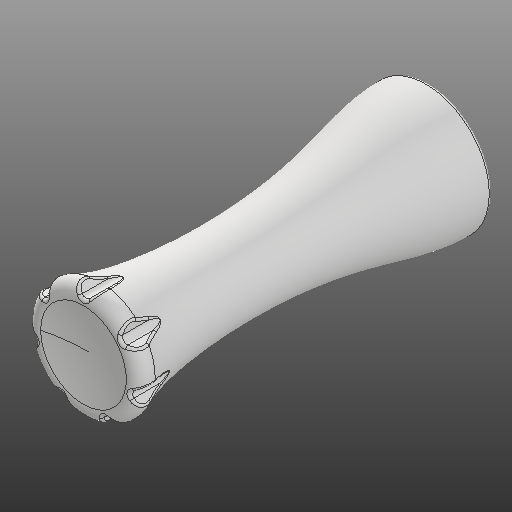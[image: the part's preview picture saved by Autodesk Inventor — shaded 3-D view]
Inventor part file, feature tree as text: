
AUTODESK INVENTOR PART (.ipt)
format: ipt  version: 2020 (Build 240168000, 168)  size: 590,336 bytes
history: native  units: in
note: dims shown in document units (in); Inventor stores cm internally (conversion verified against a paired STEP export)
features: fillet x2, sketch x2, revolve x1, extrude x1, pattern_circular x1
ambient origin geometry x8: Origin, YZ Plane, XZ Plane, XY Plane, X Axis, Y Axis, Z Axis, Center Point
bodies: Solid1 (feature_tree)
feature tree (7):
  revolve  "Revolution1"  [1 undecoded]
  extrude  "Extrusion1"  TaperAngle=90.0deg  [1 undecoded]
  pattern_circular  "Circular Pattern1"  [2 undecoded]
  fillet  "Fillet1"  Radius=0.2756in
  fillet  "Fillet3"  Radius=0.0984in
  sketch  "Sketch2"  dims[d1=0.2203in d4=0.0394in]
  sketch  "Sketch3"  dims[d6=1.1811in d7=90.0deg d10=0.0787in d11=0.2756in d12=0.0984in d13=0.6693in d14=0.0197in d15=0.1589in d16=45.0deg d17=45.0deg d18=0.0394in d19=0.1982in d24=0.3937in d25=0.0in d28=0.0197in d29=0.0098in d30=2.7559in d31=360.0deg]
note: 4 required parameter values undecoded (feature->parameter linkage not recoverable at this tier; creation-order binding heuristic only, values carry confidence <= 0.55)